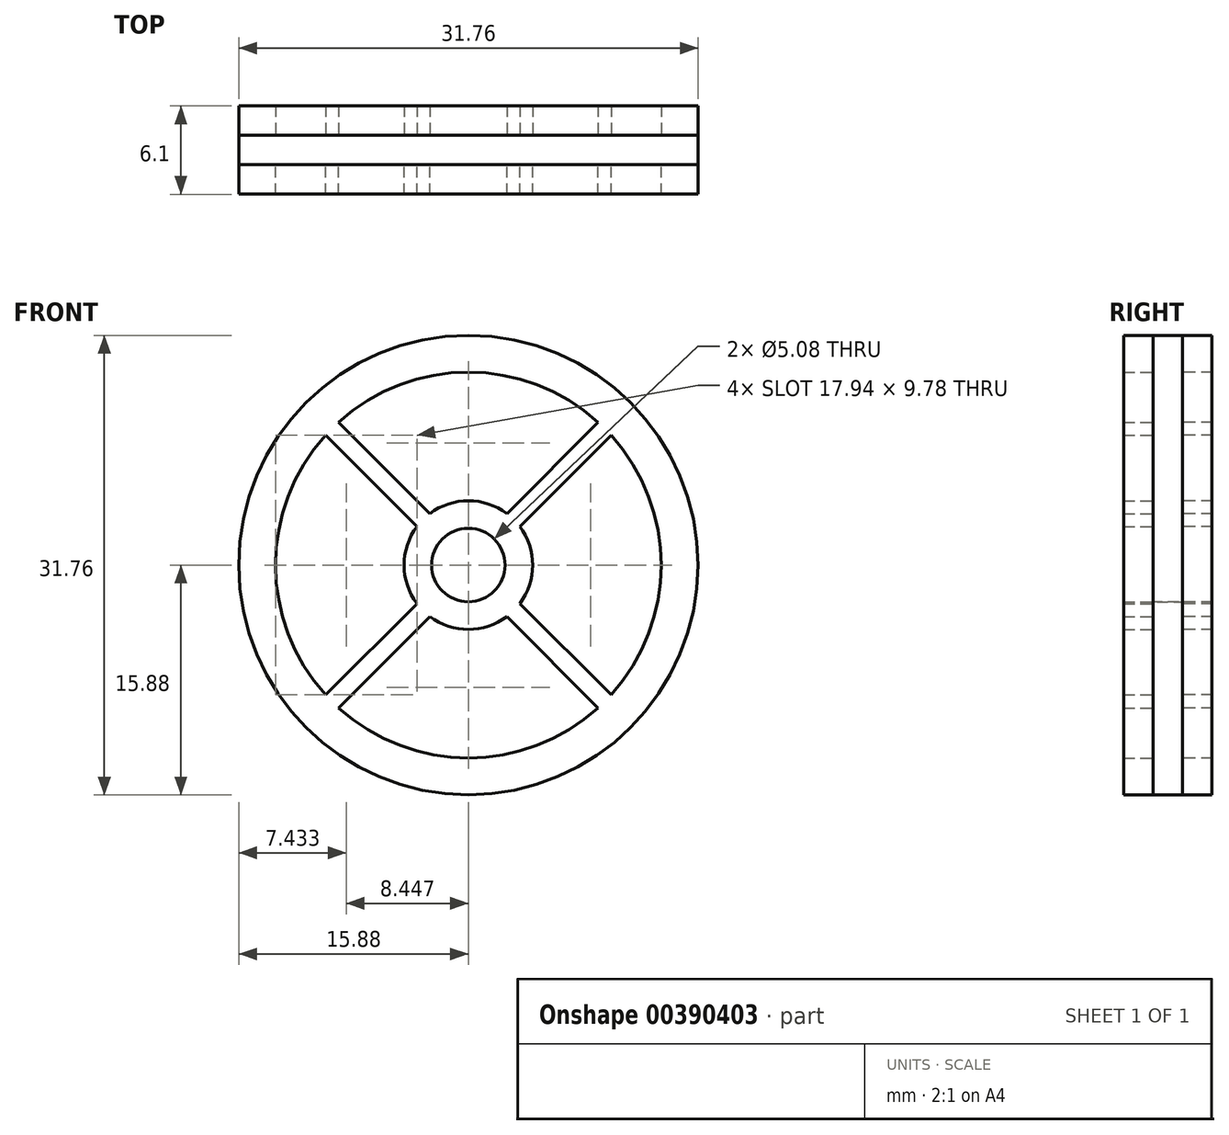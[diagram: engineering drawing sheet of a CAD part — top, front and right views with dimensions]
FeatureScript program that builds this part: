
annotation { "Feature Type Name" : "Feature", "Feature Type Description" : "" }
export const myFeature = defineFeature(function(context is Context, id is Id, definition is map)
    precondition{}
    {
        {
            var Q0;
            Q0=qCreatedBy(makeId("Front.planeOp"),FACE);
            var sketch = newSketch(context, id + "F0", { "sketchPlane" : qUnion([Q0])});
            skCircle(sketch, "E0", {"center": v(0, 0) * mm, "radius": 2.54 * mm});
            skCircle(sketch, "E1", {"center": v(0, 0) * mm, "radius": 15.87 * mm});
            skSolve(sketch);
        }
        {
            var Q0;
            Q0 = qSketchRegion(id + "F0", true);
            extrude(context, id + "F1", {"entities" : qUnion([Q0]), "depth" : 1.02 * mm});
        }
        {
            var Q0;
            Q0=makeQuery(id+"F1.opExtrude","CAP_FACE",FACE,{"disambiguationData":[OSD([sQuery(id+"F0.wireOp",EDGE,"E0"),sQuery(id+"F0.wireOp",EDGE,"E1")])],"isStart":false});
            var sketch = newSketch(context, id + "F2", { "sketchPlane" : qUnion([Q0])});
            skArc(sketch, "E2", {"start": v(-3.56, 2.66) * mm, "mid": v(-4.45, 0) * mm, "end": v(-3.56, -2.66) * mm});
            skCircle(sketch, "E3.0", {"center": v(0, 0) * mm, "radius": 2.54 * mm});
            skLineSegment(sketch, "E4", {"start": v(0, 0) * mm, "end": v(11.23, 11.23) * mm, "construction": true});
            skLineSegment(sketch, "E5", {"start": v(0, 0) * mm, "end": v(15.87, 0) * mm, "construction": true});
            skLineSegment(sketch, "E6.0", {"start": v(2.66, 3.56) * mm, "end": v(8.97, 9.87) * mm});
            skLineSegment(sketch, "E7.trimOffspring", {"start": v(3.56, 2.66) * mm, "end": v(9.87, 8.97) * mm});
            skArc(sketch, "E8", {"start": v(11.67, 10.77) * mm, "mid": v(11.23, 11.23) * mm, "end": v(10.77, 11.67) * mm});
            skCircle(sketch, "E9", {"center": v(0, 0) * mm, "radius": 15.87 * mm});
            skArc(sketch, "E10", {"start": v(8.97, 9.87) * mm, "mid": v(0, 13.33) * mm, "end": v(-8.97, 9.87) * mm});
            skLineSegment(sketch, "E11.trimOffspring", {"start": v(10.77, 11.67) * mm, "end": v(10.78, 11.67) * mm});
            skLineSegment(sketch, "E12.trimOffspring", {"start": v(11.67, 10.77) * mm, "end": v(11.67, 10.78) * mm});
            skLineSegment(sketch, "E13.1.0", {"start": v(-3.56, 2.66) * mm, "end": v(-9.87, 8.97) * mm});
            skLineSegment(sketch, "E13.1.1", {"start": v(-2.66, 3.56) * mm, "end": v(-8.97, 9.87) * mm});
            skLineSegment(sketch, "E13.2.0", {"start": v(-2.66, -3.56) * mm, "end": v(-8.97, -9.87) * mm});
            skLineSegment(sketch, "E13.2.1", {"start": v(-3.56, -2.66) * mm, "end": v(-9.87, -8.97) * mm});
            skLineSegment(sketch, "E13.3.0", {"start": v(3.56, -2.66) * mm, "end": v(9.87, -8.97) * mm});
            skLineSegment(sketch, "E13.3.1", {"start": v(2.66, -3.56) * mm, "end": v(8.97, -9.87) * mm});
            skArc(sketch, "E14.trimOffspring", {"start": v(-9.87, 8.97) * mm, "mid": v(-13.33, 0) * mm, "end": v(-9.87, -8.97) * mm});
            skArc(sketch, "E15.trimOffspring", {"start": v(-2.66, -3.56) * mm, "mid": v(0, -4.44) * mm, "end": v(2.66, -3.56) * mm});
            skArc(sketch, "E16.trimOffspring", {"start": v(-8.97, -9.87) * mm, "mid": v(0, -13.33) * mm, "end": v(8.97, -9.87) * mm});
            skArc(sketch, "E17.trimOffspring", {"start": v(3.56, -2.66) * mm, "mid": v(4.45, 0) * mm, "end": v(3.56, 2.66) * mm});
            skArc(sketch, "E18.trimOffspring", {"start": v(9.87, -8.97) * mm, "mid": v(13.33, 0) * mm, "end": v(9.87, 8.97) * mm});
            skArc(sketch, "E19.trimOffspring", {"start": v(2.66, 3.56) * mm, "mid": v(0, 4.44) * mm, "end": v(-2.66, 3.56) * mm});
            skSolve(sketch);
        }
        {
            var Q0;
            Q0 = qSketchRegion(id + "F2", true);
            extrude(context, id + "F3", {"entities" : qUnion([Q0]), "depth" : 2.03 * mm});
        }
        {
            var Q0;
            Q0=makeQuery(id+"F1.opExtrude","SWEPT_BODY",BODY,{"disambiguationData":[OSD([sQuery(id+"F0.wireOp",EDGE,"E0"),sQuery(id+"F0.wireOp",EDGE,"E1")])]});
            var Q1;
            Q1=qCreatedBy(makeId("Front.planeOp"),FACE);
            mirror(context, id + "F4", {"operationType" : NewBodyOperationType.ADD, "entities" : qUnion([Q0]), "mirrorPlane" : qUnion([Q1])});
        }
        {
            var Q0;
            Q0=makeQuery(id+"F3.opExtrude","SWEPT_BODY",BODY,{"disambiguationData":[OSD([sQuery(id+"F2.wireOp",EDGE,"E2"),sQuery(id+"F2.wireOp",EDGE,"E3.0"),sQuery(id+"F2.wireOp",EDGE,"E6.0"),sQuery(id+"F2.wireOp",EDGE,"E7.trimOffspring"),sQuery(id+"F2.wireOp",EDGE,"E9"),sQuery(id+"F2.wireOp",EDGE,"E10"),sQuery(id+"F2.wireOp",EDGE,"E13.1.0"),sQuery(id+"F2.wireOp",EDGE,"E13.1.1"),sQuery(id+"F2.wireOp",EDGE,"E13.2.0"),sQuery(id+"F2.wireOp",EDGE,"E13.2.1"),sQuery(id+"F2.wireOp",EDGE,"E13.3.0"),sQuery(id+"F2.wireOp",EDGE,"E13.3.1"),sQuery(id+"F2.wireOp",EDGE,"E14.trimOffspring"),sQuery(id+"F2.wireOp",EDGE,"E15.trimOffspring"),sQuery(id+"F2.wireOp",EDGE,"E16.trimOffspring"),sQuery(id+"F2.wireOp",EDGE,"E17.trimOffspring"),sQuery(id+"F2.wireOp",EDGE,"E18.trimOffspring"),sQuery(id+"F2.wireOp",EDGE,"E19.trimOffspring")])]});
            var Q1;
            Q1=qCreatedBy(makeId("Front.planeOp"),FACE);
            mirror(context, id + "F5", {"entities" : qUnion([Q0]), "mirrorPlane" : qUnion([Q1])});
        }
    });
